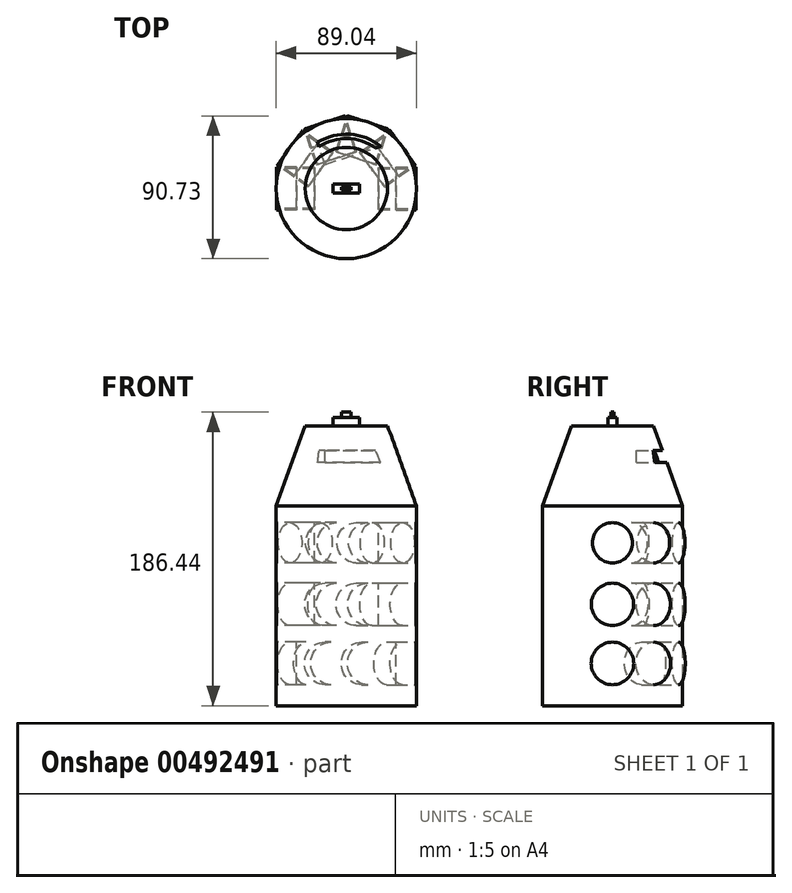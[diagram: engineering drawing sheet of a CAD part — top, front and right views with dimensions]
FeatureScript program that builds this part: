
annotation { "Feature Type Name" : "Feature", "Feature Type Description" : "" }
export const myFeature = defineFeature(function(context is Context, id is Id, definition is map)
    precondition{}
    {
        {
            var Q0;
            Q0=qCreatedBy(makeId("Top.planeOp"),FACE);
            var sketch = newSketch(context, id + "F0", { "sketchPlane" : qUnion([Q0])});
            skCircle(sketch, "E0", {"center": v(0, 0) * mm, "radius": 44.52 * mm});
            skSolve(sketch);
        }
        {
            var Q0;
            Q0=makeQuery(id+"F0.imprint","IMPRINT",FACE,{"disambiguationData":[TD([[makeQuery(id+"F0.imprint","IMPRINT",EDGE,{"derivedFrom":sQuery(id+"F0.wireOp",EDGE,"E0")}),1.0]])]});
            extrude(context, id + "F1", {"entities" : qUnion([Q0]), "depth" : 127 * mm});
        }
        {
            var Q0;
            Q0=qCreatedBy(makeId("Top.planeOp"),FACE);
            cPlane(context, id + "F2", {"entities" : qUnion([Q0]), "cplaneType" : CPlaneType.OFFSET, "offset" : 177.8 * mm, "width" : 152.4 * mm, "height" : 152.4 * mm});
        }
        {
            var Q0;
            Q0=qCreatedBy(id+"F2.planeOp",FACE);
            var sketch = newSketch(context, id + "F3", { "sketchPlane" : qUnion([Q0])});
            skCircle(sketch, "E1", {"center": v(0, 0) * mm, "radius": 26.15 * mm});
            skSolve(sketch);
        }
        {
            var Q1;
            Q1=makeQuery(id+"F1.opExtrude","CAP_FACE",FACE,{"disambiguationData":[OSD([sQuery(id+"F0.wireOp",EDGE,"E0")])],"isStart":false});
            var Q2;
            Q2=makeQuery(id+"F3.imprint","IMPRINT",FACE,{"disambiguationData":[TD([[makeQuery(id+"F3.imprint","IMPRINT",EDGE,{"derivedFrom":sQuery(id+"F3.wireOp",EDGE,"E1")}),1.0]])]});
            loft(context, id + "F4", {"operationType" : NewBodyOperationType.ADD, "sheetProfilesArray" : [{ "sheetProfileEntities" : qUnion([Q1]) }, { "sheetProfileEntities" : qUnion([Q2]) }]});
        }
        {
            var Q0;
            Q0=makeQuery(id+"F4.opLoft","CAP_FACE",FACE,{"disambiguationData":[OSD([makeQuery(id+"F3.imprint","IMPRINT",FACE,{"disambiguationData":[TD([[makeQuery(id+"F3.imprint","IMPRINT",EDGE,{"derivedFrom":sQuery(id+"F3.wireOp",EDGE,"E1")}),1.0]])]})])],"isStart":true});
            var sketch = newSketch(context, id + "F5", { "sketchPlane" : qUnion([Q0])});
            skLineSegment(sketch, "E2.bottom", {"start": v(8.51, -2.92) * mm, "end": v(-8.51, -2.92) * mm});
            skLineSegment(sketch, "E2.top", {"start": v(8.51, 2.92) * mm, "end": v(-8.51, 2.92) * mm});
            skLineSegment(sketch, "E2.left", {"start": v(8.51, -2.92) * mm, "end": v(8.51, 2.92) * mm});
            skLineSegment(sketch, "E2.right", {"start": v(-8.51, -2.92) * mm, "end": v(-8.51, 2.92) * mm});
            skPoint(sketch, "E2.middle", {"position": v(0, 0) * mm});
            skSolve(sketch);
        }
        {
            var Q0;
            Q0 = qSketchRegion(id + "F5", true);
            extrude(context, id + "F6", {"entities" : qUnion([Q0]), "operationType" : NewBodyOperationType.ADD, "depth" : 5.33 * mm});
        }
        {
            var Q0;
            Q0=makeQuery(id+"F6.opExtrude","CAP_FACE",FACE,{"disambiguationData":[OSD([sQuery(id+"F5.wireOp",EDGE,"E2.bottom"),sQuery(id+"F5.wireOp",EDGE,"E2.top"),sQuery(id+"F5.wireOp",EDGE,"E2.left"),sQuery(id+"F5.wireOp",EDGE,"E2.right")])],"isStart":false});
            var sketch = newSketch(context, id + "F7", { "sketchPlane" : qUnion([Q0])});
            skLineSegment(sketch, "E3.bottom", {"start": v(3.07, -0.93) * mm, "end": v(-3.07, -0.93) * mm});
            skLineSegment(sketch, "E3.top", {"start": v(3.07, 0.93) * mm, "end": v(-3.07, 0.93) * mm});
            skLineSegment(sketch, "E3.left", {"start": v(3.07, -0.93) * mm, "end": v(3.07, 0.93) * mm});
            skLineSegment(sketch, "E3.right", {"start": v(-3.07, -0.93) * mm, "end": v(-3.07, 0.93) * mm});
            skPoint(sketch, "E3.middle", {"position": v(0, 0) * mm});
            skSolve(sketch);
        }
        {
            var Q0;
            Q0=makeQuery(id+"F7.imprint","IMPRINT",FACE,{"disambiguationData":[TD([[makeQuery(id+"F7.imprint","IMPRINT",EDGE,{"derivedFrom":sQuery(id+"F7.wireOp",EDGE,"E3.bottom")}),-1.0]])]});
            extrude(context, id + "F8", {"entities" : qUnion([Q0]), "operationType" : NewBodyOperationType.ADD, "depth" : 3.3 * mm});
        }
        {
            var Q0;
            Q0=qCreatedBy(makeId("Right.planeOp"),FACE);
            cPlane(context, id + "F9", {"entities" : qUnion([Q0]), "cplaneType" : CPlaneType.OFFSET, "offset" : 44.2 * mm, "width" : 152.4 * mm, "height" : 152.4 * mm});
        }
        {
            var Q0;
            Q0=qCreatedBy(id+"F9.planeOp",FACE);
            var sketch = newSketch(context, id + "F10", { "sketchPlane" : qUnion([Q0])});
            skCircle(sketch, "E4", {"center": v(0, 26.85) * mm, "radius": 13.52 * mm});
            skSolve(sketch);
        }
        {
            var Q0;
            Q0 = qSketchRegion(id + "F10", true);
            extrude(context, id + "F11", {"entities" : qUnion([Q0]), "oppositeDirection" : true, "depth" : 12.7 * mm});
        }
        {
            var Q0;
            Q0=makeQuery(id+"F11.opExtrude","SWEPT_BODY",BODY,{"disambiguationData":[OSD([sQuery(id+"F10.wireOp",EDGE,"E4")])]});
            var Q1;
            {var subQ0=sQuery(id+"F0.wireOp",EDGE,"E0");Q1=makeQuery(id+"F4.boolean.opBoolean","MERGE",EDGE,{"derivedFrom":[makeQuery(id+"F1.opExtrude","CAP_EDGE",EDGE,{"disambiguationData":[OSD([subQ0])],"isStart":false}),makeQuery(id+"F4.opLoft","MID_CAP_EDGE",EDGE,{"disambiguationData":[OSD([subQ0])],"capPos":0.0})]});}
            circularPattern(context, id + "F12", {"entities" : qUnion([Q0]), "axis" : qUnion([Q1]), "angle" : 180 * degree, "instanceCount" : 6, "equalSpace" : true});
        }
        {
            var Q0;
            Q0=qCreatedBy(id+"F9.planeOp",FACE);
            var sketch = newSketch(context, id + "F13", { "sketchPlane" : qUnion([Q0])});
            skCircle(sketch, "E5", {"center": v(0, 64.38) * mm, "radius": 13.46 * mm});
            skCircle(sketch, "E6", {"center": v(0, 103.47) * mm, "radius": 12.78 * mm});
            skSolve(sketch);
        }
        {
            var Q0;
            Q0 = qSketchRegion(id + "F13", true);
            extrude(context, id + "F14", {"entities" : qUnion([Q0]), "oppositeDirection" : true, "depth" : 23.88 * mm});
        }
        {
            var Q0;
            Q0=makeQuery(id+"F14.opExtrude","SWEPT_BODY",BODY,{"disambiguationData":[OSD([sQuery(id+"F13.wireOp",EDGE,"E6")])]});
            var Q1;
            {var subQ0=sQuery(id+"F0.wireOp",EDGE,"E0");Q1=makeQuery(id+"F4.boolean.opBoolean","MERGE",EDGE,{"derivedFrom":[makeQuery(id+"F1.opExtrude","CAP_EDGE",EDGE,{"disambiguationData":[OSD([subQ0])],"isStart":false}),makeQuery(id+"F4.opLoft","MID_CAP_EDGE",EDGE,{"disambiguationData":[OSD([subQ0])],"capPos":0.0})]});}
            circularPattern(context, id + "F15", {"entities" : qUnion([Q0]), "axis" : qUnion([Q1]), "angle" : 180 * degree, "instanceCount" : 6, "equalSpace" : true});
        }
        {
            var Q0;
            Q0=makeQuery(id+"F14.opExtrude","SWEPT_BODY",BODY,{"disambiguationData":[OSD([sQuery(id+"F13.wireOp",EDGE,"E5")])]});
            var Q1;
            {var subQ0=sQuery(id+"F0.wireOp",EDGE,"E0");Q1=makeQuery(id+"F4.boolean.opBoolean","MERGE",EDGE,{"derivedFrom":[makeQuery(id+"F1.opExtrude","CAP_EDGE",EDGE,{"disambiguationData":[OSD([subQ0])],"isStart":false}),makeQuery(id+"F4.opLoft","MID_CAP_EDGE",EDGE,{"disambiguationData":[OSD([subQ0])],"capPos":0.0})]});}
            circularPattern(context, id + "F16", {"entities" : qUnion([Q0]), "axis" : qUnion([Q1]), "angle" : 180 * degree, "instanceCount" : 6, "equalSpace" : true});
        }
        {
            var Q0;
            Q0=makeQuery(id+"F15.opPattern","COPY",FACE,{"derivedFrom":makeQuery(id+"F14.opExtrude","CAP_FACE",FACE,{"disambiguationData":[OSD([sQuery(id+"F13.wireOp",EDGE,"E6")])],"isStart":true}),"instanceName":"3"});
            var sketch = newSketch(context, id + "F17", { "sketchPlane" : qUnion([Q0])});
            skLineSegment(sketch, "E7.bottom", {"start": v(8.22, 154.48) * mm, "end": v(-37.68, 154.48) * mm});
            skLineSegment(sketch, "E7.top", {"start": v(8.22, 162.23) * mm, "end": v(-37.68, 162.23) * mm});
            skLineSegment(sketch, "E7.left", {"start": v(8.22, 154.48) * mm, "end": v(8.22, 162.23) * mm});
            skLineSegment(sketch, "E7.right", {"start": v(-37.68, 154.48) * mm, "end": v(-37.68, 162.23) * mm});
            skPoint(sketch, "E7.middle", {"position": v(-14.73, 158.35) * mm});
            skSolve(sketch);
        }
        {
            var Q0;
            Q0 = qSketchRegion(id + "F17", true);
            extrude(context, id + "F18", {"entities" : qUnion([Q0]), "operationType" : NewBodyOperationType.REMOVE, "oppositeDirection" : true, "depth" : 25.4 * mm, "offsetDistance" : 25.4 * mm});
        }
    });
